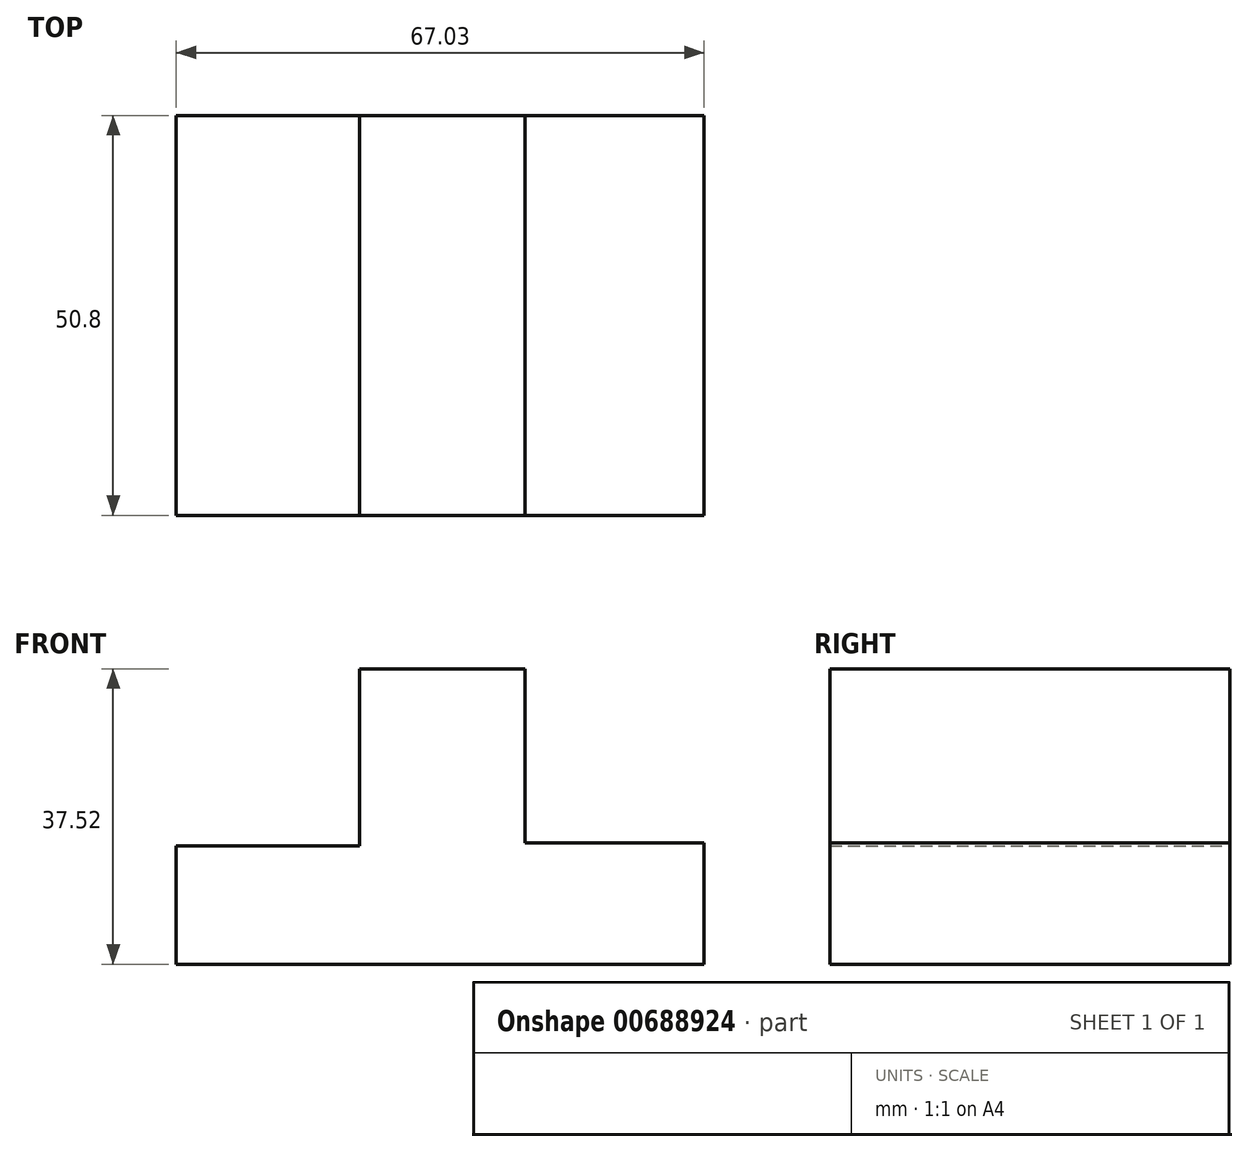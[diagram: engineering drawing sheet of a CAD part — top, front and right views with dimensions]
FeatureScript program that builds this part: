
annotation { "Feature Type Name" : "Feature", "Feature Type Description" : "" }
export const myFeature = defineFeature(function(context is Context, id is Id, definition is map)
    precondition{}
    {
        {
            var Q0;
            Q0=qCreatedBy(makeId("Front.planeOp"),FACE);
            var sketch = newSketch(context, id + "F0", { "sketchPlane" : qUnion([Q0])});
            skLineSegment(sketch, "E0", {"start": v(-38.29, 0) * mm, "end": v(-38.29, 14.99) * mm});
            skLineSegment(sketch, "E1", {"start": v(-38.29, 14.99) * mm, "end": v(-14.99, 14.99) * mm});
            skLineSegment(sketch, "E2", {"start": v(-14.99, 14.99) * mm, "end": v(-14.99, 37.52) * mm});
            skLineSegment(sketch, "E3", {"start": v(-14.99, 37.52) * mm, "end": v(6.02, 37.52) * mm});
            skLineSegment(sketch, "E4", {"start": v(6.02, 37.52) * mm, "end": v(6.02, 15.37) * mm});
            skLineSegment(sketch, "E5", {"start": v(6.02, 15.37) * mm, "end": v(28.74, 15.37) * mm});
            skLineSegment(sketch, "E6", {"start": v(28.74, 15.37) * mm, "end": v(28.74, 0) * mm});
            skLineSegment(sketch, "E7", {"start": v(28.74, 0) * mm, "end": v(-38.29, 0) * mm});
            skSolve(sketch);
        }
        {
            var Q0;
            Q0 = qSketchRegion(id + "F0", true);
            extrude(context, id + "F1", {"entities" : qUnion([Q0]), "depth" : 50.8 * mm, "offsetDistance" : 25.4 * mm});
        }
    });
